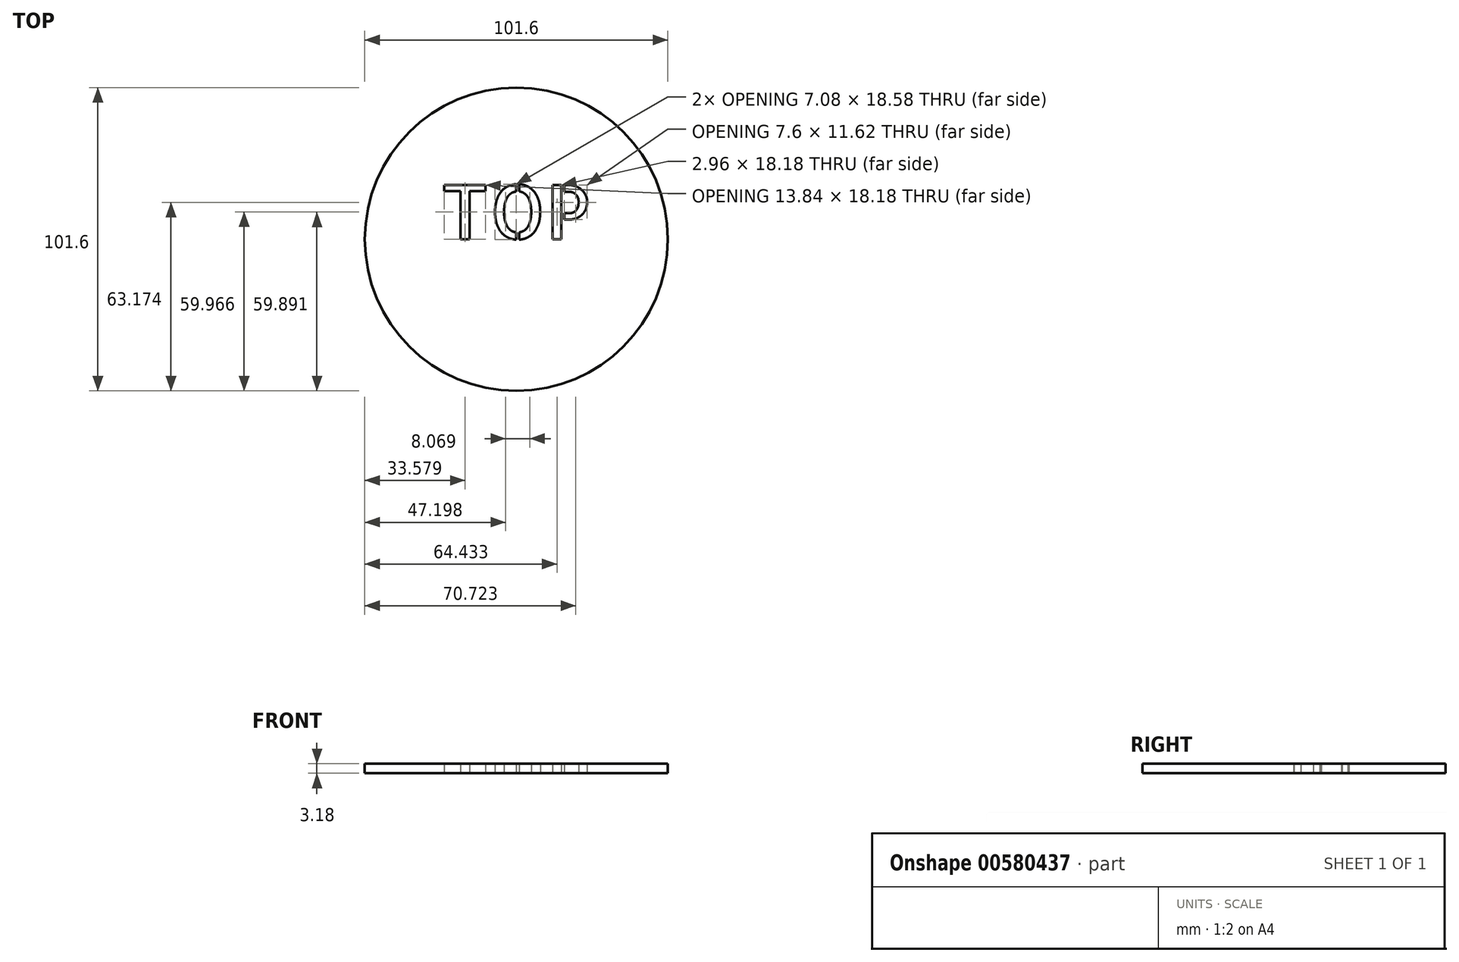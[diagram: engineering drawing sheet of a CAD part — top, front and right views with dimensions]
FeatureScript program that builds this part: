
annotation { "Feature Type Name" : "Feature", "Feature Type Description" : "" }
export const myFeature = defineFeature(function(context is Context, id is Id, definition is map)
    precondition{}
    {
        {
            var Q0;
            Q0=qCreatedBy(makeId("Top.planeOp"),FACE);
            var sketch = newSketch(context, id + "F0", { "sketchPlane" : qUnion([Q0])});
            skCircle(sketch, "E0", {"center": v(0, 0) * mm, "radius": 50.8 * mm});
            skText(sketch, "E1", { "text": "TOP", "fontName": "AllertaStencil-Regular.ttf"});
            const initialGuessF0  = {"E1": [-0.0254, 0, 1, 0, 0.01819]};
            skSetInitialGuess(sketch, initialGuessF0);
            skSolve(sketch);
        }
        {
            var Q0;
            Q0=makeQuery(id+"F0.imprint","IMPRINT",FACE,{"disambiguationData":[TD([[makeQuery(id+"F0.imprint","IMPRINT",EDGE,{"derivedFrom":sQuery(id+"F0.wireOp",EDGE,"E0")}),1.0]])]});
            extrude(context, id + "F1", {"entities" : qUnion([Q0]), "depth" : 3.17 * mm, "offsetDistance" : 25.4 * mm});
        }
    });
